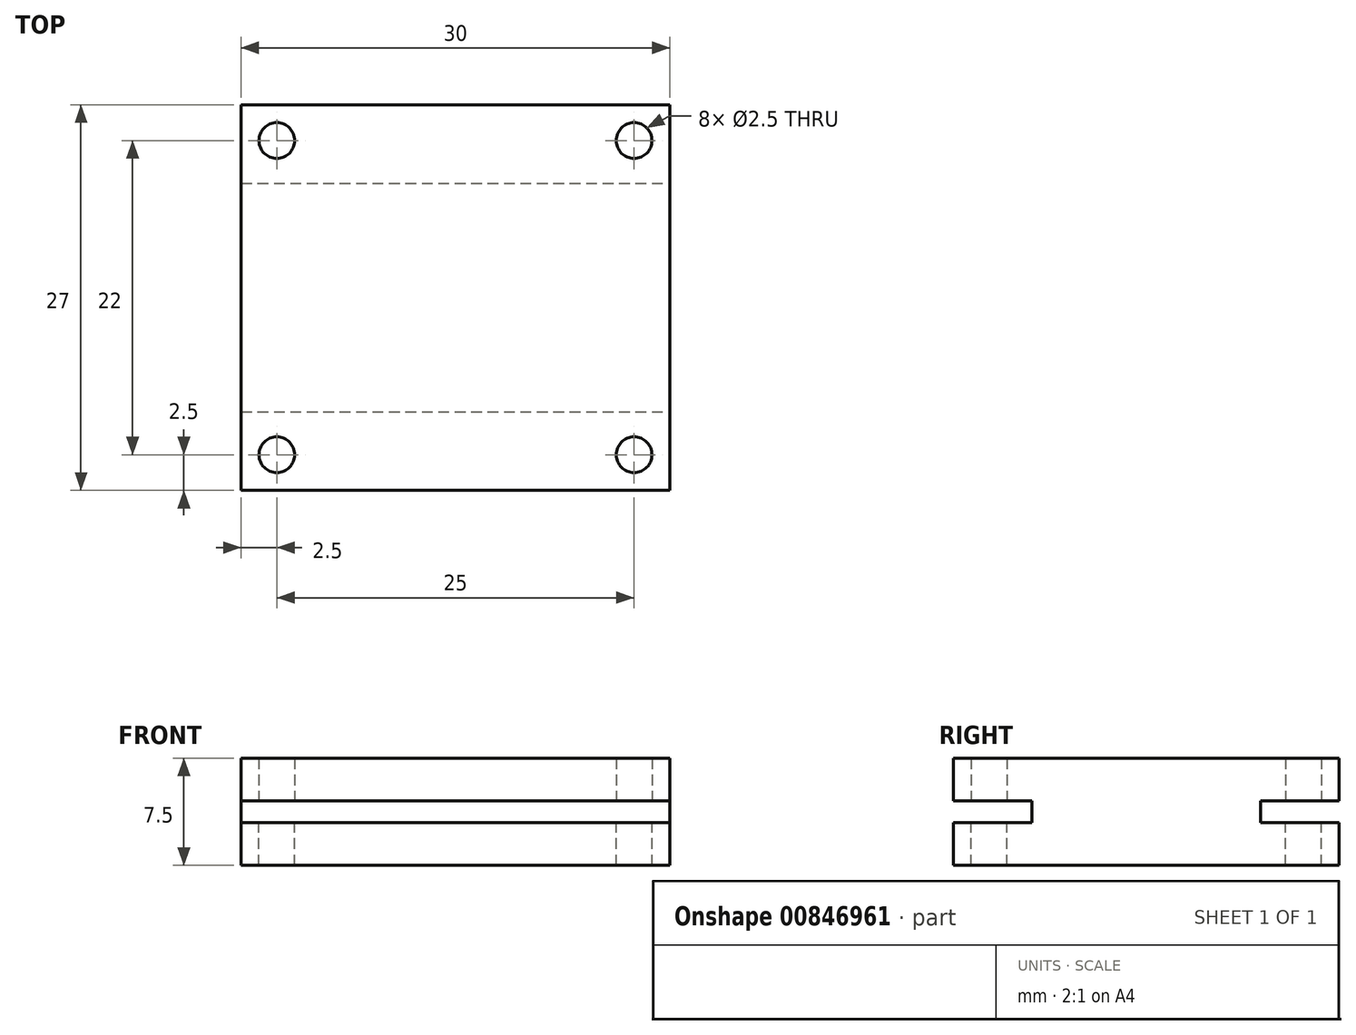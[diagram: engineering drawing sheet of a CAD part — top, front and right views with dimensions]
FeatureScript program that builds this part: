
annotation { "Feature Type Name" : "Feature", "Feature Type Description" : "" }
export const myFeature = defineFeature(function(context is Context, id is Id, definition is map)
    precondition{}
    {
        {
            var Q0;
            Q0=qCreatedBy(makeId("Top.planeOp"),FACE);
            var sketch = newSketch(context, id + "F0", { "sketchPlane" : qUnion([Q0])});
            skLineSegment(sketch, "E0.bottom", {"start": v(15, 13.5) * mm, "end": v(-15, 13.5) * mm});
            skLineSegment(sketch, "E0.top", {"start": v(15, -13.5) * mm, "end": v(-15, -13.5) * mm});
            skLineSegment(sketch, "E0.left", {"start": v(15, 13.5) * mm, "end": v(15, -13.5) * mm});
            skLineSegment(sketch, "E0.right", {"start": v(-15, 13.5) * mm, "end": v(-15, -13.5) * mm});
            skPoint(sketch, "E0.middle", {"position": v(0, 0) * mm});
            skCircle(sketch, "E1", {"center": v(-12.5, 11) * mm, "radius": 1.25 * mm});
            skCircle(sketch, "E2", {"center": v(-12.5, -11) * mm, "radius": 1.25 * mm});
            skCircle(sketch, "E3", {"center": v(12.5, 11) * mm, "radius": 1.25 * mm});
            skCircle(sketch, "E4", {"center": v(12.5, -11) * mm, "radius": 1.25 * mm});
            skSolve(sketch);
        }
        {
            var Q0;
            Q0=qCreatedBy(makeId("Front.planeOp"),FACE);
            var sketch = newSketch(context, id + "F1", { "sketchPlane" : qUnion([Q0])});
            skLineSegment(sketch, "E5.bottom", {"start": v(-15, 0) * mm, "end": v(15, 0) * mm});
            skLineSegment(sketch, "E5.top", {"start": v(-15, 1.5) * mm, "end": v(15, 1.5) * mm});
            skLineSegment(sketch, "E5.left", {"start": v(-15, 0) * mm, "end": v(-15, 1.5) * mm});
            skLineSegment(sketch, "E5.right", {"start": v(15, 0) * mm, "end": v(15, 1.5) * mm});
            skLineSegment(sketch, "E6", {"start": v(-13, 0) * mm, "end": v(-13, 1.5) * mm});
            skLineSegment(sketch, "E7", {"start": v(-11, 0) * mm, "end": v(-11, 1.5) * mm});
            skLineSegment(sketch, "E8", {"start": v(-9, 0) * mm, "end": v(-9, 1.5) * mm});
            skLineSegment(sketch, "E9", {"start": v(-7, 1.5) * mm, "end": v(-7, 0) * mm});
            skLineSegment(sketch, "E10", {"start": v(-5, 1.5) * mm, "end": v(-5, 0) * mm});
            skLineSegment(sketch, "E11", {"start": v(13, 1.5) * mm, "end": v(13, 0) * mm});
            skLineSegment(sketch, "E12", {"start": v(11, 1.5) * mm, "end": v(11, 0) * mm});
            skLineSegment(sketch, "E13", {"start": v(9, 1.5) * mm, "end": v(9, 0) * mm});
            skLineSegment(sketch, "E14", {"start": v(7, 1.5) * mm, "end": v(7, 0) * mm});
            skLineSegment(sketch, "E15", {"start": v(5, 1.5) * mm, "end": v(5, 0) * mm});
            skLineSegment(sketch, "E16", {"start": v(-15, 0) * mm, "end": v(-13, 1.5) * mm});
            skLineSegment(sketch, "E17", {"start": v(-13, 1.5) * mm, "end": v(-11, 0) * mm});
            skLineSegment(sketch, "E18", {"start": v(-11, 0) * mm, "end": v(-9, 1.5) * mm});
            skLineSegment(sketch, "E19", {"start": v(-9, 1.5) * mm, "end": v(-7, 0) * mm});
            skLineSegment(sketch, "E20", {"start": v(-7, 0) * mm, "end": v(-5, 1.5) * mm});
            skLineSegment(sketch, "E21", {"start": v(-5, 1.5) * mm, "end": v(0, 0) * mm});
            skLineSegment(sketch, "E22", {"start": v(0, 0) * mm, "end": v(5, 1.5) * mm});
            skLineSegment(sketch, "E23", {"start": v(15, 0) * mm, "end": v(13, 1.5) * mm});
            skLineSegment(sketch, "E24", {"start": v(11, 0) * mm, "end": v(13, 1.5) * mm});
            skLineSegment(sketch, "E25", {"start": v(11, 0) * mm, "end": v(9, 1.5) * mm});
            skLineSegment(sketch, "E26", {"start": v(5, 1.5) * mm, "end": v(7, 0) * mm});
            skLineSegment(sketch, "E27", {"start": v(7, 0) * mm, "end": v(9, 1.5) * mm});
            skSolve(sketch);
        }
        {
            var Q0;
            {var subQ0=sQuery(id+"F1.wireOp",EDGE,"E10");Q0=makeQuery(id+"F1.imprint","IMPRINT",FACE,{"disambiguationData":[TD([[makeQuery(id+"F1.imprint","IMPRINT",EDGE,{"derivedFrom":subQ0}),1.0]])]});}
            var Q1;
            {var subQ2=sQuery(id+"F1.wireOp",EDGE,"E10");Q1=makeQuery(id+"F1.imprint","IMPRINT",FACE,{"disambiguationData":[TD([[makeQuery(id+"F1.imprint","IMPRINT",EDGE,{"derivedFrom":subQ2}),-1.0]])]});}
            var Q2;
            {var subQ0=sQuery(id+"F1.wireOp",EDGE,"E8");Q2=makeQuery(id+"F1.imprint","IMPRINT",FACE,{"disambiguationData":[TD([[makeQuery(id+"F1.imprint","IMPRINT",EDGE,{"derivedFrom":subQ0}),-1.0]])]});}
            var Q3;
            {var subQ2=sQuery(id+"F1.wireOp",EDGE,"E8");Q3=makeQuery(id+"F1.imprint","IMPRINT",FACE,{"disambiguationData":[TD([[makeQuery(id+"F1.imprint","IMPRINT",EDGE,{"derivedFrom":subQ2}),1.0]])]});}
            var Q4;
            {var subQ0=sQuery(id+"F1.wireOp",EDGE,"E6");Q4=makeQuery(id+"F1.imprint","IMPRINT",FACE,{"disambiguationData":[TD([[makeQuery(id+"F1.imprint","IMPRINT",EDGE,{"derivedFrom":subQ0}),-1.0]])]});}
            var Q5;
            {var subQ2=sQuery(id+"F1.wireOp",EDGE,"E6");Q5=makeQuery(id+"F1.imprint","IMPRINT",FACE,{"disambiguationData":[TD([[makeQuery(id+"F1.imprint","IMPRINT",EDGE,{"derivedFrom":subQ2}),1.0]])]});}
            var Q6;
            {var subQ0=sQuery(id+"F1.wireOp",EDGE,"E15");Q6=makeQuery(id+"F1.imprint","IMPRINT",FACE,{"disambiguationData":[TD([[makeQuery(id+"F1.imprint","IMPRINT",EDGE,{"derivedFrom":subQ0}),-1.0]])]});}
            var Q7;
            {var subQ2=sQuery(id+"F1.wireOp",EDGE,"E15");Q7=makeQuery(id+"F1.imprint","IMPRINT",FACE,{"disambiguationData":[TD([[makeQuery(id+"F1.imprint","IMPRINT",EDGE,{"derivedFrom":subQ2}),1.0]])]});}
            var Q8;
            {var subQ0=sQuery(id+"F1.wireOp",EDGE,"E13");Q8=makeQuery(id+"F1.imprint","IMPRINT",FACE,{"disambiguationData":[TD([[makeQuery(id+"F1.imprint","IMPRINT",EDGE,{"derivedFrom":subQ0}),-1.0]])]});}
            var Q9;
            {var subQ2=sQuery(id+"F1.wireOp",EDGE,"E13");Q9=makeQuery(id+"F1.imprint","IMPRINT",FACE,{"disambiguationData":[TD([[makeQuery(id+"F1.imprint","IMPRINT",EDGE,{"derivedFrom":subQ2}),1.0]])]});}
            var Q10;
            {var subQ0=sQuery(id+"F1.wireOp",EDGE,"E11");Q10=makeQuery(id+"F1.imprint","IMPRINT",FACE,{"disambiguationData":[TD([[makeQuery(id+"F1.imprint","IMPRINT",EDGE,{"derivedFrom":subQ0}),-1.0]])]});}
            var Q11;
            {var subQ2=sQuery(id+"F1.wireOp",EDGE,"E11");Q11=makeQuery(id+"F1.imprint","IMPRINT",FACE,{"disambiguationData":[TD([[makeQuery(id+"F1.imprint","IMPRINT",EDGE,{"derivedFrom":subQ2}),1.0]])]});}
            extrude(context, id + "F2", {"entities" : qUnion([Q0, Q1, Q2, Q3, Q4, Q5, Q6, Q7, Q8, Q9, Q10, Q11]), "endBound" : BoundingType.SYMMETRIC, "depth" : 16 * mm, "offsetDistance" : 25 * mm});
        }
        {
            var Q0;
            Q0=makeQuery(id+"F0.imprint","IMPRINT",FACE,{"disambiguationData":[TD([[makeQuery(id+"F0.imprint","IMPRINT",EDGE,{"derivedFrom":sQuery(id+"F0.wireOp",EDGE,"E0.bottom")}),1.0]])]});
            extrude(context, id + "F3", {"entities" : qUnion([Q0]), "operationType" : NewBodyOperationType.ADD, "oppositeDirection" : true, "depth" : 3 * mm, "offsetDistance" : 25 * mm});
        }
        {
            var Q0;
            {var subQ0=sQuery(id+"F1.wireOp",EDGE,"E5.left");Q0=makeQuery(id+"F1.imprint","IMPRINT",FACE,{"disambiguationData":[TD([[makeQuery(id+"F1.imprint","IMPRINT",EDGE,{"derivedFrom":subQ0}),-1.0]])]});}
            var Q1;
            {var subQ2=sQuery(id+"F1.wireOp",EDGE,"E7");Q1=makeQuery(id+"F1.imprint","IMPRINT",FACE,{"disambiguationData":[TD([[makeQuery(id+"F1.imprint","IMPRINT",EDGE,{"derivedFrom":subQ2}),1.0]])]});}
            var Q2;
            {var subQ0=sQuery(id+"F1.wireOp",EDGE,"E7");Q2=makeQuery(id+"F1.imprint","IMPRINT",FACE,{"disambiguationData":[TD([[makeQuery(id+"F1.imprint","IMPRINT",EDGE,{"derivedFrom":subQ0}),-1.0]])]});}
            var Q3;
            {var subQ2=sQuery(id+"F1.wireOp",EDGE,"E9");Q3=makeQuery(id+"F1.imprint","IMPRINT",FACE,{"disambiguationData":[TD([[makeQuery(id+"F1.imprint","IMPRINT",EDGE,{"derivedFrom":subQ2}),-1.0]])]});}
            var Q4;
            {var subQ0=sQuery(id+"F1.wireOp",EDGE,"E9");Q4=makeQuery(id+"F1.imprint","IMPRINT",FACE,{"disambiguationData":[TD([[makeQuery(id+"F1.imprint","IMPRINT",EDGE,{"derivedFrom":subQ0}),1.0]])]});}
            var Q5;
            {var subQ0=sQuery(id+"F1.wireOp",EDGE,"E21");Q5=makeQuery(id+"F1.imprint","IMPRINT",FACE,{"disambiguationData":[TD([[makeQuery(id+"F1.imprint","IMPRINT",EDGE,{"derivedFrom":subQ0}),1.0]])]});}
            var Q6;
            {var subQ0=sQuery(id+"F1.wireOp",EDGE,"E14");Q6=makeQuery(id+"F1.imprint","IMPRINT",FACE,{"disambiguationData":[TD([[makeQuery(id+"F1.imprint","IMPRINT",EDGE,{"derivedFrom":subQ0}),-1.0]])]});}
            var Q7;
            {var subQ2=sQuery(id+"F1.wireOp",EDGE,"E14");Q7=makeQuery(id+"F1.imprint","IMPRINT",FACE,{"disambiguationData":[TD([[makeQuery(id+"F1.imprint","IMPRINT",EDGE,{"derivedFrom":subQ2}),1.0]])]});}
            var Q8;
            {var subQ0=sQuery(id+"F1.wireOp",EDGE,"E12");Q8=makeQuery(id+"F1.imprint","IMPRINT",FACE,{"disambiguationData":[TD([[makeQuery(id+"F1.imprint","IMPRINT",EDGE,{"derivedFrom":subQ0}),-1.0]])]});}
            var Q9;
            {var subQ2=sQuery(id+"F1.wireOp",EDGE,"E12");Q9=makeQuery(id+"F1.imprint","IMPRINT",FACE,{"disambiguationData":[TD([[makeQuery(id+"F1.imprint","IMPRINT",EDGE,{"derivedFrom":subQ2}),1.0]])]});}
            var Q10;
            {var subQ0=sQuery(id+"F1.wireOp",EDGE,"E5.right");Q10=makeQuery(id+"F1.imprint","IMPRINT",FACE,{"disambiguationData":[TD([[makeQuery(id+"F1.imprint","IMPRINT",EDGE,{"derivedFrom":subQ0}),1.0]])]});}
            extrude(context, id + "F4", {"entities" : qUnion([Q0, Q1, Q2, Q3, Q4, Q5, Q6, Q7, Q8, Q9, Q10]), "endBound" : BoundingType.SYMMETRIC, "depth" : 16 * mm, "offsetDistance" : 25 * mm});
        }
        {
            var Q0;
            Q0=makeQuery(id+"F0.imprint","IMPRINT",FACE,{"disambiguationData":[TD([[makeQuery(id+"F0.imprint","IMPRINT",EDGE,{"derivedFrom":sQuery(id+"F0.wireOp",EDGE,"E0.bottom")}),1.0]])]});
            extrude(context, id + "F5", {"entities" : qUnion([Q0]), "operationType" : NewBodyOperationType.ADD, "depth" : 4.5 * mm, "offsetDistance" : 25 * mm, "hasSecondDirection" : true, "secondDirectionOppositeDirection" : false, "secondDirectionDepth" : 1.5 * mm});
        }
    });
